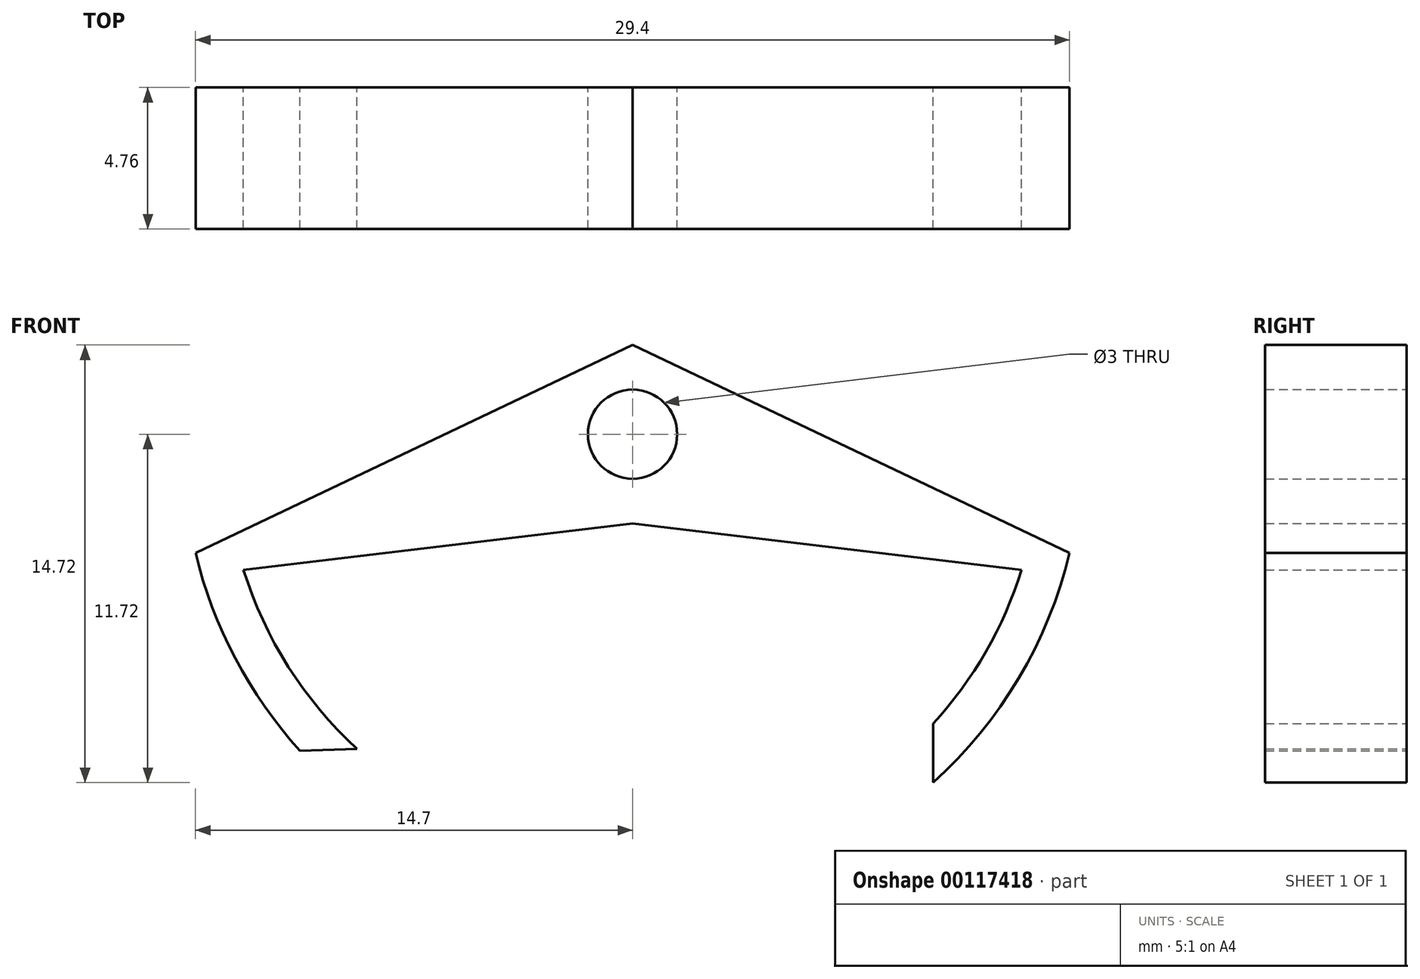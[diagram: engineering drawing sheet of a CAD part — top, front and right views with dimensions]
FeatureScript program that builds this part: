
annotation { "Feature Type Name" : "Feature", "Feature Type Description" : "" }
export const myFeature = defineFeature(function(context is Context, id is Id, definition is map)
    precondition{}
    {
        {
            var Q0;
            Q0=qCreatedBy(makeId("Front.planeOp"),FACE);
            var sketch = newSketch(context, id + "F0", { "sketchPlane" : qUnion([Q0])});
            skLineSegment(sketch, "E0", {"start": v(0, -0.48) * mm, "end": v(0, -0.48) * mm});
            skArc(sketch, "E1", {"start": v(10.1, -11.72) * mm, "mid": v(13, -8.2) * mm, "end": v(14.7, -4) * mm});
            skArc(sketch, "E2", {"start": v(10.1, -9.74) * mm, "mid": v(11.88, -7.31) * mm, "end": v(13.09, -4.56) * mm});
            skLineSegment(sketch, "E3", {"start": v(10.1, -9.74) * mm, "end": v(10.1, -11.72) * mm});
            skArc(sketch, "E4.trimOffspring", {"start": v(-13.09, -4.56) * mm, "mid": v(-11.58, -7.82) * mm, "end": v(-9.27, -10.58) * mm});
            skArc(sketch, "E5.trimOffspring", {"start": v(-14.7, -4) * mm, "mid": v(-13.36, -7.54) * mm, "end": v(-11.18, -10.65) * mm});
            skPoint(sketch, "E6.orphan", {"position": v(-14.43, -4.97) * mm});
            skPoint(sketch, "E7.orphan", {"position": v(14.43, -4.97) * mm});
            skCircle(sketch, "E8", {"center": v(0, 0) * mm, "radius": 1.5 * mm});
            skLineSegment(sketch, "E9", {"start": v(-13.09, -4.56) * mm, "end": v(0, -3) * mm});
            skLineSegment(sketch, "E10", {"start": v(0, -3) * mm, "end": v(13.09, -4.56) * mm});
            skLineSegment(sketch, "E11", {"start": v(-14.7, -4) * mm, "end": v(0, 3) * mm});
            skLineSegment(sketch, "E12", {"start": v(0, 3) * mm, "end": v(14.7, -4) * mm});
            skLineSegment(sketch, "E13", {"start": v(-11.18, -10.65) * mm, "end": v(-9.27, -10.58) * mm});
            skLineSegment(sketch, "E14", {"start": v(10.1, -11.72) * mm, "end": v(10.05, -9.95) * mm});
            skSolve(sketch);
        }
        {
            var Q0;
            Q0 = qSketchRegion(id + "F0", true);
            extrude(context, id + "F1", {"entities" : qUnion([Q0]), "depth" : 4.76 * mm});
        }
    });
